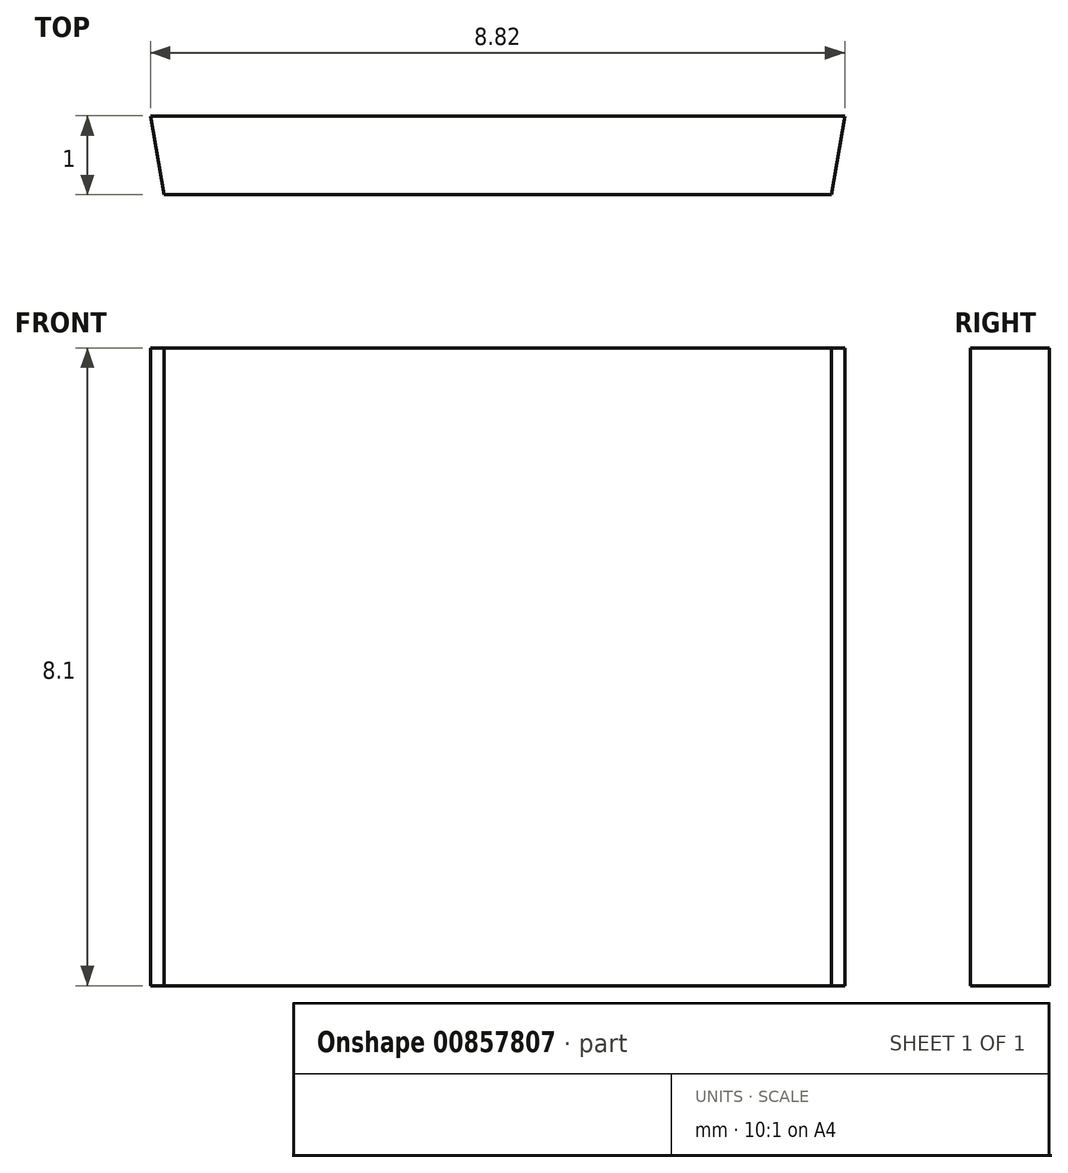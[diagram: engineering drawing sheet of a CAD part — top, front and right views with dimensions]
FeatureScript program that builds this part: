
annotation { "Feature Type Name" : "Feature", "Feature Type Description" : "" }
export const myFeature = defineFeature(function(context is Context, id is Id, definition is map)
    precondition{}
    {
        {
            var Q0;
            Q0=qCreatedBy(makeId("Top.planeOp"),FACE);
            var sketch = newSketch(context, id + "F0", { "sketchPlane" : qUnion([Q0])});
            skLineSegment(sketch, "E0", {"start": v(-1.95, 4.22) * mm, "end": v(6.87, 4.22) * mm});
            skPoint(sketch, "E1", {"position": v(2.46, 4.22) * mm});
            skLineSegment(sketch, "E2", {"start": v(-1.78, 3.22) * mm, "end": v(6.7, 3.22) * mm});
            skPoint(sketch, "E3", {"position": v(2.46, 3.22) * mm});
            skLineSegment(sketch, "E4", {"start": v(-1.95, 4.22) * mm, "end": v(-1.78, 3.22) * mm});
            skLineSegment(sketch, "E5", {"start": v(6.87, 4.22) * mm, "end": v(6.7, 3.22) * mm});
            skSolve(sketch);
        }
        {
            var Q0;
            Q0 = qSketchRegion(id + "F0", true);
            extrude(context, id + "F1", {"entities" : qUnion([Q0]), "depth" : 8.1 * mm, "offsetDistance" : 25 * mm});
        }
    });
